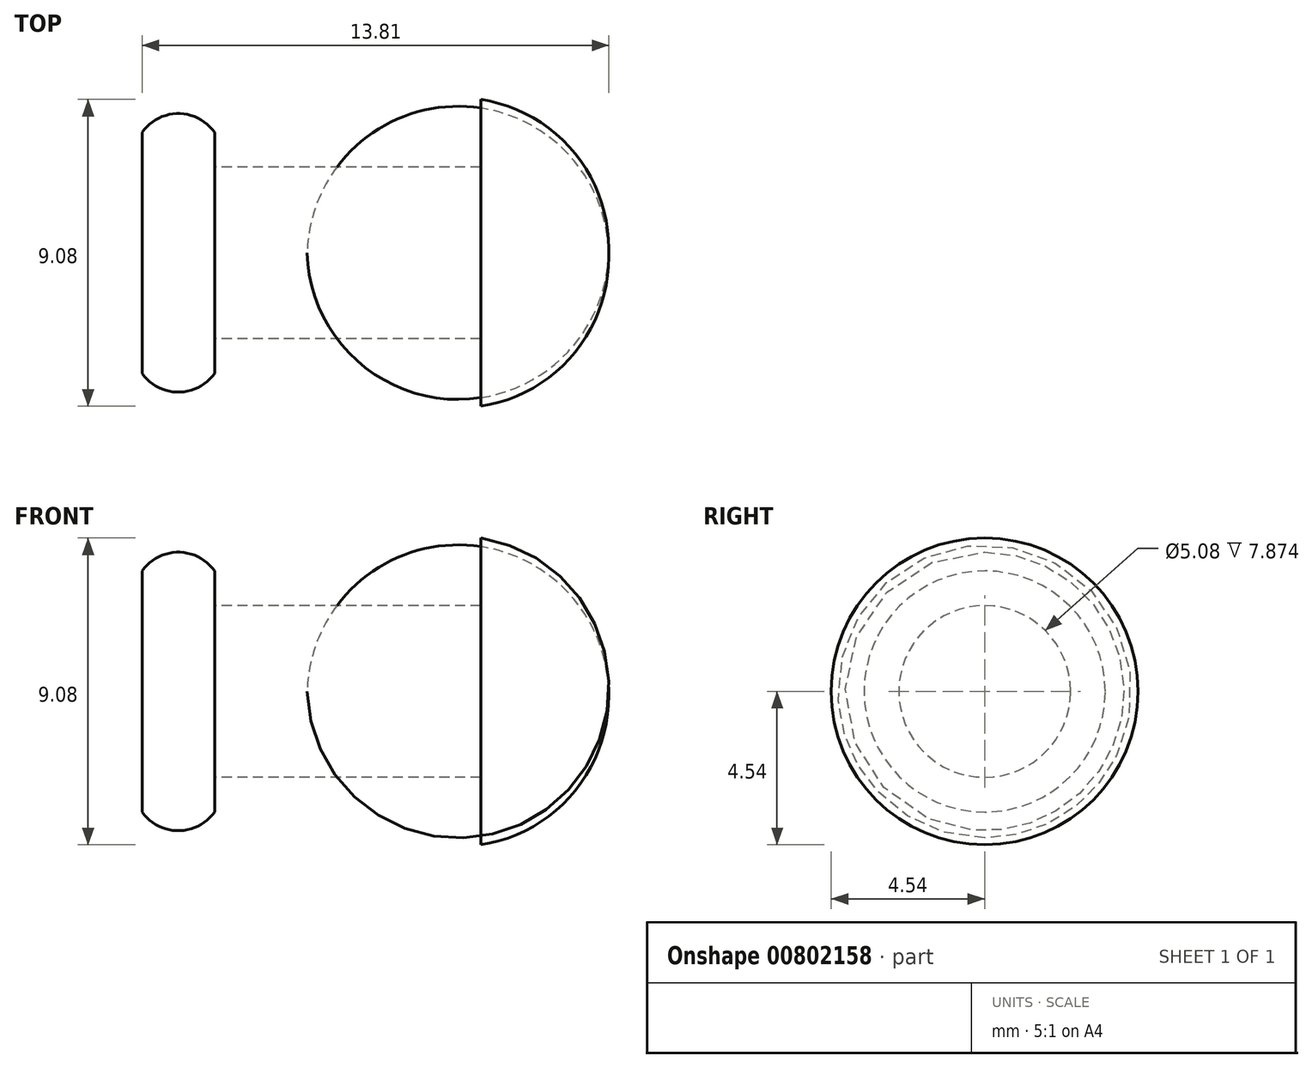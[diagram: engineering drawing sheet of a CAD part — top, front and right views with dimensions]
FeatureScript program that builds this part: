
annotation { "Feature Type Name" : "Feature", "Feature Type Description" : "" }
export const myFeature = defineFeature(function(context is Context, id is Id, definition is map)
    precondition{}
    {
        {
            var Q0;
            Q0=qCreatedBy(makeId("Front.planeOp"),FACE);
            var sketch = newSketch(context, id + "F0", { "sketchPlane" : qUnion([Q0])});
            skLineSegment(sketch, "E0", {"start": v(-0.44, 2.54) * mm, "end": v(7.43, 2.54) * mm});
            skLineSegment(sketch, "E1", {"start": v(7.43, 2.54) * mm, "end": v(7.43, 4.54) * mm});
            skLineSegment(sketch, "E2", {"start": v(-0.44, 2.54) * mm, "end": v(-0.44, 3.57) * mm});
            skArc(sketch, "E3", {"start": v(-0.44, 3.57) * mm, "mid": v(-1.51, 4.12) * mm, "end": v(-2.58, 3.57) * mm});
            skLineSegment(sketch, "E4", {"start": v(0, 0) * mm, "end": v(14.33, 0) * mm, "construction": true});
            skPoint(sketch, "E5", {"position": v(11.22, 0) * mm});
            skArc(sketch, "E6", {"start": v(11.22, 0) * mm, "mid": v(10.19, 2.99) * mm, "end": v(7.43, 4.54) * mm});
            skLineSegment(sketch, "E7", {"start": v(-2.58, 0) * mm, "end": v(11.22, 0) * mm});
            skLineSegment(sketch, "E8", {"start": v(-2.58, 3.57) * mm, "end": v(-2.58, 0) * mm});
            skSolve(sketch);
        }
        {
            var Q0;
            Q0=qSketchRegion(id+"F0",true);
            var Q1;
            Q1=sQuery(id+"F0.wireOp",EDGE,"E4");
            revolve(context, id + "F1", {"entities" : qUnion([Q0]), "axis" : qUnion([Q1]), "revolveType" : RevolveType.FULL});
        }
    });
